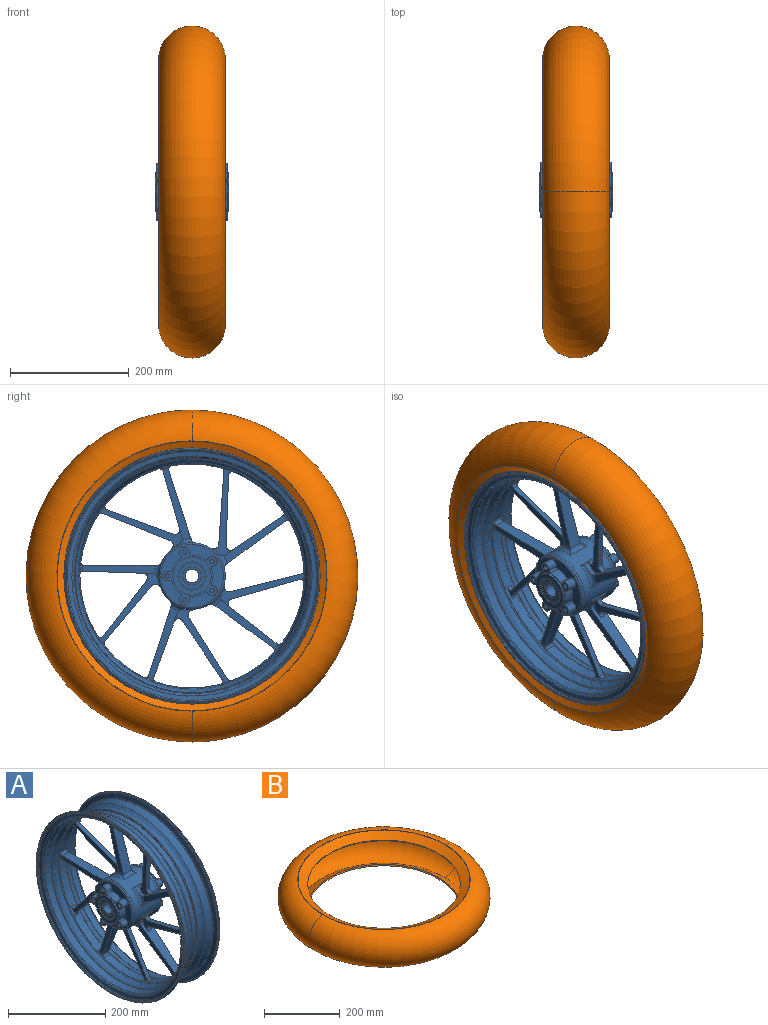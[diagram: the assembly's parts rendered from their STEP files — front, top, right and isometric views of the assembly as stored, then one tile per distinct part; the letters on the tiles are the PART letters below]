
ASSEMBLY  parts=2 mates=1
PART A: 286 faces, bbox 125.2x468.5x468.5 mm
  f0: cylinder r=11.66mm len=120.31mm, axis (1,0,0), area 8812.2mm2, adj f1,f2
  f1: plane 30.78x30.78mm, normal (1,0,0), area 317mm2, adj f0,f3
  f2: plane 30.78x30.78mm, normal (-1,0,0), area 317mm2, adj f0,f4
  f3: cylinder r=15.39mm len=30.78mm, axis (1,0,0), area 9mm2, adj f1,f5
  f4: cylinder r=15.39mm len=30.78mm, axis (-1,0,0), area 9mm2, adj f2,f6
  f5: plane 41.97x41.97mm, normal (1,0,0), area 639.4mm2, adj f3,f7
  f6: plane 41.97x41.97mm, normal (-1,0,0), area 639.4mm2, adj f4,f8
  f7: cylinder r=20.98mm len=41.97mm, axis (1,0,0), area 12.3mm2, adj f5,f9
  f8: cylinder r=20.98mm len=41.97mm, axis (-1,0,0), area 12.3mm2, adj f6,f10
  f9: plane 48.5x48.5mm, normal (1,0,0), area 463.8mm2, adj f7,f11
  f10: plane 48.5x48.5mm, normal (-1,0,0), area 463.8mm2, adj f8,f12
  f11: cylinder r=24.25mm len=48.5mm, axis (1,0,0), area 284.2mm2, adj f9,f13
  f12: cylinder r=24.25mm len=48.5mm, axis (1,0,0), area 284.2mm2, adj f10,f19
  f13: plane 64.35x64.35mm, normal (1,0,0), area 1405.2mm2, adj f11,f25
  f14: plane 7.46x7.46mm, normal (1,0,0), area 43.7mm2, adj f26
  f15: plane 7.46x7.46mm, normal (1,0,0), area 43.7mm2, adj f27
  f16: plane 7.46x7.46mm, normal (1,0,0), area 43.7mm2, adj f28
  f17: plane 7.46x7.46mm, normal (1,0,0), area 43.7mm2, adj f29
  f18: plane 7.46x7.46mm, normal (1,0,0), area 43.7mm2, adj f30,f31
  f19: plane 64.35x64.35mm, normal (-1,0,0), area 1405.2mm2, adj f12,f32
  f20: plane 7.46x7.46mm, normal (-1,0,0), area 43.7mm2, adj f33
  f21: plane 7.46x7.46mm, normal (-1,0,0), area 43.7mm2, adj f34
  f22: plane 7.46x7.46mm, normal (-1,0,0), area 43.7mm2, adj f35
  f23: plane 7.46x7.46mm, normal (-1,0,0), area 43.7mm2, adj f36
  f24: plane 7.46x7.46mm, normal (-1,0,0), area 43.7mm2, adj f37,f38
  f25: cylinder r=32.18mm len=64.35mm, axis (1,0,0), area 565.6mm2, adj f13,f39
  f26: cylinder r=3.73mm len=16.79mm, axis (-1,0,0), area 393.5mm2, adj f14,f39
  f27: cylinder r=3.73mm len=16.79mm, axis (-1,0,0), area 393.5mm2, adj f15,f39
  f28: cylinder r=3.73mm len=16.79mm, axis (-1,0,0), area 393.5mm2, adj f16,f39
  f29: cylinder r=3.73mm len=16.79mm, axis (-1,0,0), area 393.5mm2, adj f17,f39
  f30: cylinder r=3.73mm len=16.79mm, axis (-1,0,0), area 196.7mm2, adj f18,f31,f39
  f31: cylinder r=3.73mm len=16.79mm, axis (-1,0,0), area 196.7mm2, adj f18,f30,f39
  f32: cylinder r=32.18mm len=64.35mm, axis (1,0,0), area 565.6mm2, adj f19,f40
  f33: cylinder r=3.73mm len=16.79mm, axis (-1,0,0), area 393.5mm2, adj f20,f40
  f34: cylinder r=3.73mm len=16.79mm, axis (-1,0,0), area 393.5mm2, adj f21,f40
  f35: cylinder r=3.73mm len=16.79mm, axis (-1,0,0), area 393.5mm2, adj f22,f40
  f36: cylinder r=3.73mm len=16.79mm, axis (-1,0,0), area 393.5mm2, adj f23,f40
  f37: cylinder r=3.73mm len=16.79mm, axis (-1,0,0), area 196.7mm2, adj f24,f38,f40
  f38: cylinder r=3.73mm len=16.79mm, axis (-1,0,0), area 196.7mm2, adj f24,f37,f40
  f39: plane 96.61x92.71mm, normal (1,0,0), area 1483.4mm2, adj f25,f26,f27,f28,f29,f30,f31,f41
  f40: plane 96.61x92.71mm, normal (-1,0,0), area 1483.4mm2, adj f32,f33,f34,f35,f36,f37,f38,f63
  f41: cylinder r=34.97mm len=20.3mm, axis (1,0,0), area 430.9mm2, adj f39,f42,f62,f85
  f42: cylinder r=2.8mm len=16.79mm, axis (-1,0,0), area 46.7mm2, adj f39,f41,f43,f85
  f43: cylinder r=2.8mm len=16.79mm, axis (-1,0,0), area 38.8mm2, adj f39,f42,f44,f85
  f44: cylinder r=8.39mm len=16.79mm, axis (-1,0,0), area 116.4mm2, adj f39,f43,f45,f85
  f45: cylinder r=8.39mm len=16.79mm, axis (-1,0,0), area 470.5mm2, adj f39,f44,f46,f85
  f46: cylinder r=2.8mm len=16.79mm, axis (1,0,0), area 85.5mm2, adj f39,f45,f47,f85
  f47: cylinder r=34.97mm len=23.87mm, axis (1,0,0), area 430.9mm2, adj f39,f46,f48,f85
  f48: cylinder r=2.8mm len=16.79mm, axis (-1,0,0), area 85.5mm2, adj f39,f47,f49,f85
  f49: cylinder r=8.39mm len=16.79mm, axis (-1,0,0), area 586.8mm2, adj f39,f48,f50,f85
  f50: cylinder r=2.8mm len=16.79mm, axis (1,0,0), area 85.5mm2, adj f39,f49,f51,f85
  f51: cylinder r=34.97mm len=25.1mm, axis (1,0,0), area 430.9mm2, adj f39,f50,f52,f85
  f52: cylinder r=2.8mm len=16.79mm, axis (-1,0,0), area 85.5mm2, adj f39,f51,f53,f85
  f53: cylinder r=8.39mm len=16.79mm, axis (-1,0,0), area 586.8mm2, adj f39,f52,f54,f85
  f54: cylinder r=2.8mm len=16.79mm, axis (1,0,0), area 85.5mm2, adj f39,f53,f55,f85
  f55: cylinder r=34.97mm len=23.87mm, axis (1,0,0), area 430.9mm2, adj f39,f54,f56,f85
  f56: cylinder r=2.8mm len=16.79mm, axis (-1,0,0), area 85.5mm2, adj f39,f55,f57,f85
  f57: cylinder r=8.39mm len=16.79mm, axis (-1,0,0), area 586.8mm2, adj f39,f56,f58,f85
  f58: cylinder r=2.8mm len=16.79mm, axis (1,0,0), area 85.5mm2, adj f39,f57,f59,f85
  f59: cylinder r=34.97mm len=20.3mm, axis (1,0,0), area 430.9mm2, adj f39,f58,f60,f85
  f60: cylinder r=2.8mm len=16.79mm, axis (-1,0,0), area 85.5mm2, adj f39,f59,f61,f85
  f61: cylinder r=8.39mm len=16.79mm, axis (-1,0,0), area 586.8mm2, adj f39,f60,f62,f85
  f62: cylinder r=2.8mm len=16.79mm, axis (1,0,0), area 85.5mm2, adj f39,f41,f61,f85
  f63: cylinder r=34.97mm len=20.3mm, axis (1,0,0), area 430.9mm2, adj f40,f64,f84,f86
  f64: cylinder r=2.8mm len=16.79mm, axis (1,0,0), area 85.5mm2, adj f40,f63,f65,f86
  f65: cylinder r=8.39mm len=16.79mm, axis (-1,0,0), area 586.8mm2, adj f40,f64,f66,f86
  f66: cylinder r=2.8mm len=16.79mm, axis (-1,0,0), area 85.5mm2, adj f40,f65,f67,f86
  f67: cylinder r=34.97mm len=20.3mm, axis (1,0,0), area 430.9mm2, adj f40,f66,f68,f86
  f68: cylinder r=2.8mm len=16.79mm, axis (1,0,0), area 85.5mm2, adj f40,f67,f69,f86
  f69: cylinder r=8.39mm len=16.79mm, axis (-1,0,0), area 586.8mm2, adj f40,f68,f70,f86
  f70: cylinder r=2.8mm len=16.79mm, axis (-1,0,0), area 85.5mm2, adj f40,f69,f71,f86
  f71: cylinder r=34.97mm len=23.87mm, axis (1,0,0), area 430.9mm2, adj f40,f70,f72,f86
  f72: cylinder r=2.8mm len=16.79mm, axis (1,0,0), area 85.5mm2, adj f40,f71,f73,f86
  f73: cylinder r=8.39mm len=16.79mm, axis (-1,0,0), area 586.8mm2, adj f40,f72,f74,f86
  f74: cylinder r=2.8mm len=16.79mm, axis (-1,0,0), area 85.5mm2, adj f40,f73,f75,f86
  f75: cylinder r=34.97mm len=25.1mm, axis (1,0,0), area 430.9mm2, adj f40,f74,f76,f86
  f76: cylinder r=2.8mm len=16.79mm, axis (1,0,0), area 85.5mm2, adj f40,f75,f77,f86
  f77: cylinder r=8.39mm len=16.79mm, axis (-1,0,0), area 586.8mm2, adj f40,f76,f78,f86
  f78: cylinder r=2.8mm len=16.79mm, axis (-1,0,0), area 85.5mm2, adj f40,f77,f79,f86
  f79: cylinder r=34.97mm len=23.87mm, axis (1,0,0), area 430.9mm2, adj f40,f78,f80,f86
  f80: cylinder r=2.8mm len=16.79mm, axis (1,0,0), area 85.5mm2, adj f40,f79,f81,f86
  f81: cylinder r=8.39mm len=16.79mm, axis (-1,0,0), area 470.5mm2, adj f40,f80,f82,f86
  f82: cylinder r=8.39mm len=16.79mm, axis (-1,0,0), area 116.4mm2, adj f40,f81,f83,f86
  f83: cylinder r=2.8mm len=16.79mm, axis (-1,0,0), area 38.8mm2, adj f40,f82,f84,f86
  f84: cylinder r=2.8mm len=16.79mm, axis (-1,0,0), area 46.7mm2, adj f40,f63,f83,f86
  f85: plane 106.32x106.32mm, normal (1,0,0), area 3921.2mm2, adj f41,f42,f43,f44,f45,f46,f47,f48
  f86: plane 106.32x106.32mm, normal (-1,0,0), area 3921.2mm2, adj f63,f64,f65,f66,f67,f68,f69,f70
  f87: torus R=53.16mm, axis (1,0,0), area 758.5mm2, adj f85,f89,f91
  f88: torus R=53.16mm, axis (-1,0,0), area 758.5mm2, adj f86,f90,f92
  f89: torus R=53.16mm, axis (1,0,0), area 758.5mm2, adj f85,f87,f91
  f90: torus R=53.16mm, axis (-1,0,0), area 758.5mm2, adj f86,f88,f92
  f91: cylinder r=55.96mm len=111.91mm, axis (1,0,0), area 1639.5mm2, adj f87,f89,f104
  f92: cylinder r=55.96mm len=111.91mm, axis (1,0,0), area 1639.5mm2, adj f88,f90,f104
  f93: cylinder r=9.33mm len=37.91mm, axis (1,0,0), area 325.9mm2, adj f104,f105,f111,f112
  f94: plane 39.04x4.28mm, normal (0,0.94,0.34), area 104.7mm2, adj f96,f104,f114,f116,f117,f123
  f95: cylinder r=9.33mm len=37.91mm, axis (1,0,0), area 325.9mm2, adj f96,f104,f123,f124
  f96: torus R=63.42mm, axis (-1,0,0), area 325.2mm2, adj f94,f95,f104,f114,f115,f124,f133
  f97: plane 39.04x4.48mm, normal (0,-0.03,1), area 104.7mm2, adj f99,f104,f126,f128,f129,f136
  f98: cylinder r=9.33mm len=37.91mm, axis (1,0,0), area 325.9mm2, adj f99,f104,f136,f150
  f99: torus R=63.42mm, axis (-1,0,0), area 325.2mm2, adj f97,f98,f104,f129,f130,f149,f150
  f100: plane 39.04x4.35mm, normal (0,-0.96,0.28), area 104.7mm2, adj f102,f104,f138,f140,f141,f152
  f101: cylinder r=9.33mm len=37.91mm, axis (1,0,0), area 325.9mm2, adj f102,f104,f152,f163
  f102: torus R=63.42mm, axis (-1,0,0), area 325.2mm2, adj f100,f101,f104,f138,f139,f162,f163
  f103: plane 39.04x3.9mm, normal (0,-0.56,-0.83), area 104.7mm2, adj f104,f108,f154,f157,f158,f166
  f104: cylinder r=55.96mm len=111.91mm, axis (1,0,0), area 16231.7mm2, adj f91,f92,f93,f94,f95,f96,f97,f98
  f105: torus R=63.42mm, axis (-1,0,0), area 325.2mm2, adj f93,f104,f106,f112,f113,f168,f169
  f106: plane 39.04x3.78mm, normal (0,0.61,-0.79), area 104.7mm2, adj f104,f105,f111,f168,f171,f172
  f107: cylinder r=9.33mm len=37.91mm, axis (1,0,0), area 325.9mm2, adj f104,f108,f166,f182
  f108: torus R=63.42mm, axis (-1,0,0), area 325.3mm2, adj f103,f104,f107,f158,f159,f181,f182
  f109: torus R=194.62mm, axis (1,0,0), area 1109.6mm2, adj f110,f145,f183
  f110: torus R=194.62mm, axis (1,0,0), area 1109.6mm2, adj f109,f179,f183
  f111: torus R=63.42mm, axis (-1,0,0), area 325.2mm2, adj f93,f104,f106,f112,f172,f173,f184
  f112: plane 122.38x23.27mm, normal (0,0,1), area 2498.4mm2, adj f93,f105,f111,f113,f184,f185
  f113: cone r=0mm half-angle=88.7deg, axis (1,0,0), area 1400.3mm2, adj f105,f112,f147,f169,f174,f185,f186
  f114: cylinder r=57.79mm len=11.72mm, axis (-1,0,0), area 126.5mm2, adj f94,f96,f115,f187
  f115: cylinder r=9.33mm len=11.19mm, axis (-1,0,0), area 105.7mm2, adj f96,f114,f125,f133,f187
  f116: cylinder r=7.46mm len=12.25mm, axis (-1,0,0), area 138mm2, adj f94,f121,f187,f189
  f117: cylinder r=57.79mm len=11.72mm, axis (-1,0,0), area 126.5mm2, adj f94,f122,f123,f189
  f118: cylinder r=7.46mm len=10.01mm, axis (1,0,0), area 153mm2, adj f119,f125,f187,f189
  f119: plane 112.57x40.97mm, normal (0,-0.34,0.94), area 1117.3mm2, adj f118,f120,f187,f189
  f120: cylinder r=5.6mm len=9.33mm, axis (1,0,0), area 63.8mm2, adj f119,f187,f188,f189
  f121: plane 115x46.46mm, normal (0,0.37,-0.93), area 1156.7mm2, adj f116,f187,f189,f190
  f122: cylinder r=9.33mm len=11.19mm, axis (-1,0,0), area 105.7mm2, adj f117,f123,f125,f189,f192
  f123: torus R=63.42mm, axis (-1,0,0), area 325.2mm2, adj f94,f95,f104,f117,f122,f124,f192
  f124: plane 116.39x37.82mm, normal (0,-0.95,0.31), area 2498.4mm2, adj f95,f96,f123,f133,f134,f192
  f125: plane 113x33.11mm, normal (0,0.96,-0.28), area 2219.2mm2, adj f115,f118,f122,f133,f187,f189,f192,f193
  f126: cylinder r=57.79mm len=9.84mm, axis (-1,0,0), area 126.5mm2, adj f97,f135,f136,f194
  f127: plane 123.73x9.33mm, normal (0,1,0.07), area 1156.7mm2, adj f128,f194,f195,f196
  f128: cylinder r=7.46mm len=10.9mm, axis (-1,0,0), area 138mm2, adj f97,f127,f194,f196
  f129: cylinder r=57.79mm len=9.84mm, axis (-1,0,0), area 126.5mm2, adj f97,f99,f130,f196
  f130: cylinder r=9.33mm len=12.31mm, axis (-1,0,0), area 105.7mm2, adj f99,f129,f137,f149,f196
  f131: cylinder r=7.46mm len=11.63mm, axis (1,0,0), area 153mm2, adj f132,f137,f194,f196
  f132: plane 119.73x9.33mm, normal (0,-1,-0.03), area 1117.3mm2, adj f131,f194,f196,f197
  f133: cone r=0mm half-angle=88.7deg, axis (1,0,0), area 1400.3mm2, adj f96,f115,f124,f125,f134,f146,f193,f198
  f134: cylinder r=5.6mm len=17.75mm, axis (1,0,0), area 31.1mm2, adj f124,f133,f192,f198
  f135: cylinder r=9.33mm len=12.31mm, axis (-1,0,0), area 105.7mm2, adj f126,f136,f137,f194,f199
  f136: torus R=63.42mm, axis (-1,0,0), area 325.2mm2, adj f97,f98,f104,f126,f135,f150,f199
  f137: plane 97.6x66.15mm, normal (0,0.56,0.83), area 2219.2mm2, adj f130,f131,f135,f149,f194,f196,f199,f200
  f138: cylinder r=57.79mm len=12.18mm, axis (-1,0,0), area 126.5mm2, adj f100,f102,f139,f201
  f139: cylinder r=9.33mm len=12.23mm, axis (-1,0,0), area 105.7mm2, adj f102,f138,f153,f162,f201
  f140: cylinder r=7.46mm len=9.33mm, axis (-1,0,0), area 138mm2, adj f100,f144,f201,f203
  f141: cylinder r=57.79mm len=12.18mm, axis (-1,0,0), area 126.5mm2, adj f100,f151,f152,f203
  f142: cylinder r=7.46mm len=13.05mm, axis (1,0,0), area 153mm2, adj f143,f153,f201,f203
  f143: plane 115.16x33.02mm, normal (0,-0.28,-0.96), area 1117.3mm2, adj f142,f201,f202,f203
  f144: plane 120.35x30.01mm, normal (0,0.24,0.97), area 1156.7mm2, adj f140,f201,f203,f204
  f145: torus R=214.38mm, axis (1,0,0), area 8984mm2, adj f109,f179,f205
  f146: revolved ~21.47x8.32mm, area 56.3mm2, adj f133,f193,f198,f205
  f147: torus R=185.69mm, axis (1,0,0), area 49mm2, adj f113,f185,f186,f191,f205
  f148: revolved ~19.81x14.05mm, area 56.3mm2, adj f149,f200,f205,f206
  f149: cone r=0mm half-angle=88.7deg, axis (1,0,0), area 1400.3mm2, adj f99,f130,f137,f148,f150,f200,f206
  f150: plane 99x71.93mm, normal (0,-0.59,-0.81), area 2498.4mm2, adj f98,f99,f136,f149,f199,f206
  f151: cylinder r=9.33mm len=12.23mm, axis (-1,0,0), area 105.7mm2, adj f141,f152,f153,f203,f207
  f152: torus R=63.42mm, axis (-1,0,0), area 325.2mm2, adj f100,f101,f104,f141,f151,f163,f207
  f153: plane 92.82x72.73mm, normal (0,-0.62,0.79), area 2219.2mm2, adj f139,f142,f151,f162,f201,f203,f207,f208
  f154: cylinder r=57.79mm len=13.33mm, axis (-1,0,0), area 126.5mm2, adj f103,f165,f166,f209
  f155: plane 105.19x65.73mm, normal (0,-0.85,0.53), area 1156.7mm2, adj f156,f209,f210,f211
  f156: cylinder r=7.46mm len=9.33mm, axis (-1,0,0), area 60.7mm2, adj f155,f157,f209,f211
  f157: cylinder r=7.46mm len=9.33mm, axis (-1,0,0), area 77.3mm2, adj f103,f156,f209,f211
  f158: cylinder r=57.79mm len=13.33mm, axis (-1,0,0), area 126.5mm2, adj f103,f108,f159,f211
  f159: cylinder r=9.33mm len=10.94mm, axis (-1,0,0), area 105.7mm2, adj f108,f158,f164,f181,f211
  f160: cylinder r=7.46mm len=13.2mm, axis (1,0,0), area 153mm2, adj f161,f164,f209,f211
  f161: plane 99.32x66.99mm, normal (0,0.83,-0.56), area 1117.3mm2, adj f160,f209,f211,f212
  f162: cone r=0mm half-angle=88.7deg, axis (1,0,0), area 1400.3mm2, adj f102,f139,f153,f163,f178,f208,f213
  f163: plane 99x71.93mm, normal (0,0.59,-0.81), area 2498.4mm2, adj f101,f102,f152,f162,f207,f213
  f164: plane 109.5x39.86mm, normal (0,-0.94,-0.34), area 2219.2mm2, adj f159,f160,f165,f167,f181,f209,f211,f214
  f165: cylinder r=9.33mm len=10.94mm, axis (-1,0,0), area 105.7mm2, adj f154,f164,f166,f209,f214
  f166: torus R=63.42mm, axis (-1,0,0), area 325.5mm2, adj f103,f104,f107,f154,f165,f182,f214
  f167: cylinder r=5.6mm len=17.73mm, axis (1,0,0), area 34.5mm2, adj f164,f181,f214,f215
  f168: cylinder r=57.79mm len=13.17mm, axis (-1,0,0), area 126.5mm2, adj f105,f106,f169,f216
  f169: cylinder r=9.33mm len=9.4mm, axis (-1,0,0), area 105.7mm2, adj f105,f113,f168,f174,f216
  f170: plane 95.01x79.73mm, normal (0,-0.77,-0.64), area 1156.7mm2, adj f171,f177,f216,f218
  f171: cylinder r=7.46mm len=12.4mm, axis (-1,0,0), area 138mm2, adj f106,f170,f216,f218
  f172: cylinder r=57.79mm len=13.17mm, axis (-1,0,0), area 126.5mm2, adj f106,f111,f173,f218
  f173: cylinder r=9.33mm len=9.4mm, axis (-1,0,0), area 105.7mm2, adj f111,f172,f174,f184,f218
  f174: plane 117.45x23.83mm, normal (0,0.03,-1), area 2219.2mm2, adj f113,f169,f173,f175,f184,f186,f216,f218
  f175: cylinder r=7.46mm len=12.05mm, axis (1,0,0), area 153mm2, adj f174,f176,f216,f218
  f176: plane 94.4x73.76mm, normal (0,0.79,0.62), area 1117.3mm2, adj f175,f216,f217,f218
  f177: cylinder r=5.6mm len=9.33mm, axis (1,0,0), area 36.4mm2, adj f170,f216,f218,f219
  f178: revolved ~18.41x16.22mm, area 56.3mm2, adj f162,f208,f213,f220
  f179: torus R=214.38mm, axis (1,0,0), area 8984mm2, adj f110,f145,f220
  f180: revolved ~20.97x11.05mm, area 56.3mm2, adj f181,f215,f220,f221
  f181: cone r=0mm half-angle=88.7deg, axis (1,0,0), area 1438.6mm2, adj f108,f159,f164,f167,f180,f182,f215,f221
  f182: plane 116.39x37.82mm, normal (0,0.95,0.31), area 2498.4mm2, adj f107,f108,f166,f181,f214,f221
  f183: cone r=0mm half-angle=5deg, axis (-1,0,0), area 20053.6mm2, adj f109,f110,f222,f223
  f184: cone r=0mm half-angle=88.7deg, axis (-1,0,0), area 1400.3mm2, adj f111,f112,f173,f174,f185,f186,f224
  f185: cylinder r=5.6mm len=19.52mm, axis (1,0,0), area 160.6mm2, adj f112,f113,f147,f184,f191,f224
  f186: cylinder r=5.6mm len=19.59mm, axis (1,0,0), area 163.5mm2, adj f113,f147,f174,f184,f224,f233
  f187: plane 141.68x73.36mm, normal (-1,0,0), area 1648.3mm2, adj f114,f115,f116,f118,f119,f120,f121,f125
  f188: cylinder r=5.6mm len=9.33mm, axis (1,0,0), area 36mm2, adj f120,f187,f189,f225
  f189: plane 141.68x73.36mm, normal (1,0,0), area 1648.3mm2, adj f116,f117,f118,f119,f120,f121,f122,f125
  f190: cylinder r=5.6mm len=9.33mm, axis (1,0,0), area 71.8mm2, adj f121,f187,f189,f225
  f191: cylinder r=5.6mm len=19.59mm, axis (1,0,0), area 14mm2, adj f147,f185,f224,f225
  f192: cone r=0mm half-angle=88.7deg, axis (-1,0,0), area 1400.3mm2, adj f122,f123,f124,f125,f134,f193,f198,f226
  f193: cylinder r=5.6mm len=19.59mm, axis (1,0,0), area 163.5mm2, adj f125,f133,f146,f192,f225,f226
  f194: plane 148.01x35.2mm, normal (1,0,0), area 1648.3mm2, adj f126,f127,f128,f131,f132,f135,f137,f195
  f195: cylinder r=5.6mm len=9.33mm, axis (1,0,0), area 71.8mm2, adj f127,f194,f196,f227
  f196: plane 148.01x35.2mm, normal (-1,0,0), area 1648.3mm2, adj f127,f128,f129,f130,f131,f132,f137,f195
  f197: cylinder r=5.6mm len=9.33mm, axis (1,0,0), area 99.8mm2, adj f132,f194,f196,f227
  f198: cylinder r=5.6mm len=19.59mm, axis (1,0,0), area 142.9mm2, adj f133,f134,f146,f192,f226,f227
  f199: cone r=0mm half-angle=88.7deg, axis (-1,0,0), area 1400.3mm2, adj f135,f136,f137,f150,f200,f206,f228
  f200: cylinder r=5.6mm len=19.59mm, axis (1,0,0), area 163.5mm2, adj f137,f148,f149,f199,f227,f228
  f201: plane 140.98x61.17mm, normal (-1,0,0), area 1648.3mm2, adj f138,f139,f140,f142,f143,f144,f153,f202
  f202: cylinder r=5.6mm len=9.33mm, axis (1,0,0), area 99.8mm2, adj f143,f201,f203,f229
  f203: plane 140.98x61.17mm, normal (1,0,0), area 1648.3mm2, adj f140,f141,f142,f143,f144,f151,f153,f202
  f204: cylinder r=5.6mm len=9.33mm, axis (1,0,0), area 71.8mm2, adj f144,f201,f203,f229
  f205: torus R=188.06mm, axis (-1,0,0), area 1972.6mm2, adj f145,f146,f147,f148,f220,f225,f227,f229
  f206: cylinder r=5.6mm len=19.59mm, axis (1,0,0), area 174.1mm2, adj f148,f149,f150,f199,f228,f229
  f207: cone r=0mm half-angle=88.7deg, axis (-1,0,0), area 1400.3mm2, adj f151,f152,f153,f163,f208,f213,f230
  f208: cylinder r=5.6mm len=19.59mm, axis (1,0,0), area 163.5mm2, adj f153,f162,f178,f207,f229,f230
  f209: plane 126.95x96.79mm, normal (1,0,0), area 1648.3mm2, adj f154,f155,f156,f157,f160,f161,f164,f165
  f210: cylinder r=5.6mm len=9.33mm, axis (1,0,0), area 71.8mm2, adj f155,f209,f211,f231
  f211: plane 126.95x96.79mm, normal (-1,0,0), area 1648.3mm2, adj f155,f156,f157,f158,f159,f160,f161,f164
  f212: cylinder r=5.6mm len=9.33mm, axis (1,0,0), area 99.8mm2, adj f161,f209,f211,f231
  f213: cylinder r=5.6mm len=19.59mm, axis (1,0,0), area 174.1mm2, adj f162,f163,f178,f207,f230,f231
  f214: cone r=0mm half-angle=88.7deg, axis (-1,0,0), area 1438.6mm2, adj f164,f165,f166,f167,f182,f215,f221,f232
  f215: cylinder r=5.6mm len=19.59mm, axis (1,0,0), area 128.9mm2, adj f167,f180,f181,f214,f231,f232
  f216: plane 122.94x104.33mm, normal (-1,0,0), area 1648.3mm2, adj f168,f169,f170,f171,f174,f175,f176,f177
  f217: cylinder r=5.6mm len=9.33mm, axis (1,0,0), area 99.8mm2, adj f176,f216,f218,f233
  f218: plane 122.94x104.33mm, normal (1,0,0), area 1648.3mm2, adj f170,f171,f172,f173,f174,f175,f176,f177
  f219: cylinder r=5.6mm len=9.33mm, axis (1,0,0), area 35.3mm2, adj f177,f216,f218,f233
  f220: torus R=188.06mm, axis (-1,0,0), area 1972.6mm2, adj f178,f179,f180,f205,f229,f231,f233
  f221: cylinder r=5.6mm len=19.59mm, axis (1,0,0), area 174.1mm2, adj f180,f181,f182,f214,f232,f233
  f222: torus R=203.46mm, axis (1,0,0), area 3736.6mm2, adj f183,f223,f234
  f223: torus R=203.46mm, axis (1,0,0), area 3736.6mm2, adj f183,f222,f234
  f224: revolved ~21.48x4.79mm, area 49mm2, adj f184,f185,f186,f191,f235
  f225: cylinder r=188.85mm len=156.32mm, axis (1,0,0), area 4032.6mm2, adj f187,f188,f189,f190,f191,f193,f205,f235
  f226: revolved ~21.47x8.32mm, area 56.3mm2, adj f192,f193,f198,f235
  f227: cylinder r=188.85mm len=189.3mm, axis (1,0,0), area 4032.6mm2, adj f194,f195,f196,f197,f198,f200,f205,f235
  f228: revolved ~19.81x14.05mm, area 56.3mm2, adj f199,f200,f206,f235
  f229: cylinder r=188.85mm len=203.75mm, axis (1,0,0), area 4032.6mm2, adj f201,f202,f203,f204,f205,f206,f208,f220
  f230: revolved ~18.41x16.22mm, area 56.3mm2, adj f207,f208,f213,f236
  f231: cylinder r=188.85mm len=198.26mm, axis (1,0,0), area 4032.6mm2, adj f209,f210,f211,f212,f213,f215,f220,f236
  f232: revolved ~20.97x11.05mm, area 56.3mm2, adj f214,f215,f221,f236
  f233: cylinder r=188.85mm len=173.36mm, axis (1,0,0), area 4032.6mm2, adj f186,f205,f216,f217,f218,f219,f220,f221
  f234: cone r=0mm half-angle=78deg, axis (-1,0,0), area 9889.1mm2, adj f222,f223,f237,f238
  f235: torus R=188.06mm, axis (-1,0,0), area 1972.6mm2, adj f224,f225,f226,f227,f228,f229,f233,f236
  f236: torus R=188.06mm, axis (-1,0,0), area 1972.6mm2, adj f229,f230,f231,f232,f233,f235,f240
  f237: torus R=209.37mm, axis (1,0,0), area 2529.4mm2, adj f234,f238,f241
  f238: torus R=209.37mm, axis (1,0,0), area 2529.4mm2, adj f234,f237,f241
  f239: torus R=214.38mm, axis (1,0,0), area 8984mm2, adj f235,f240,f242
  f240: torus R=214.38mm, axis (1,0,0), area 8984mm2, adj f236,f239,f243
  f241: cylinder r=212.17mm len=424.34mm, axis (1,0,0), area 739.6mm2, adj f237,f238,f244
  f242: torus R=194.62mm, axis (1,0,0), area 1109.6mm2, adj f239,f243,f245
  f243: torus R=194.62mm, axis (1,0,0), area 1109.6mm2, adj f240,f242,f245
  f244: plane 428.07x428.07mm, normal (-1,0,0), area 2107.6mm2, adj f241,f246,f247
  f245: cone r=0mm half-angle=5deg, axis (1,0,0), area 20053.6mm2, adj f242,f243,f248,f249
  f246: torus R=214.03mm, axis (-1,0,0), area 1980.9mm2, adj f244,f247,f250
  f247: torus R=214.03mm, axis (-1,0,0), area 1980.9mm2, adj f244,f246,f251
  f248: torus R=203.46mm, axis (1,0,0), area 3736.6mm2, adj f245,f249,f252
  f249: torus R=203.46mm, axis (1,0,0), area 3736.6mm2, adj f245,f248,f252
  f250: torus R=214.97mm, axis (-1,0,0), area 992.1mm2, adj f246,f251,f253
  f251: torus R=214.97mm, axis (-1,0,0), area 992.1mm2, adj f247,f250,f253
  f252: cone r=0mm half-angle=78deg, axis (1,0,0), area 9889.1mm2, adj f248,f249,f254,f255
  f253: cylinder r=214.97mm len=429.93mm, axis (1,0,0), area 1050.5mm2, adj f250,f251,f256,f257
  f254: torus R=209.37mm, axis (1,0,0), area 2529.4mm2, adj f252,f255,f258
  f255: torus R=209.37mm, axis (1,0,0), area 2529.4mm2, adj f252,f254,f258
  f256: torus R=213.1mm, axis (-1,0,0), area 1710.7mm2, adj f253,f257,f259
  f257: torus R=213.1mm, axis (-1,0,0), area 1710.7mm2, adj f253,f256,f259
  f258: cylinder r=212.17mm len=424.34mm, axis (1,0,0), area 739.6mm2, adj f254,f255,f260
  f259: cone r=0mm half-angle=78deg, axis (-1,0,0), area 13941.2mm2, adj f256,f257,f261,f262
  f260: plane 428.07x428.07mm, normal (1,0,0), area 2107.6mm2, adj f258,f263,f264
  f261: torus R=203.46mm, axis (1,0,0), area 1509.3mm2, adj f259,f262,f265
  f262: torus R=203.46mm, axis (1,0,0), area 1509.3mm2, adj f259,f261,f265
  f263: torus R=214.03mm, axis (1,0,0), area 1980.9mm2, adj f260,f264,f266
  f264: torus R=214.03mm, axis (1,0,0), area 1980.9mm2, adj f260,f263,f267
  f265: cone r=0mm half-angle=5deg, axis (-1,0,0), area 22824.3mm2, adj f261,f262,f268,f269
  f266: torus R=214.97mm, axis (1,0,0), area 992.1mm2, adj f263,f267,f270
  f267: torus R=214.97mm, axis (1,0,0), area 992.1mm2, adj f264,f266,f270
  f268: torus R=214.38mm, axis (1,0,0), area 10414.5mm2, adj f265,f269,f271
  f269: torus R=214.38mm, axis (1,0,0), area 10414.5mm2, adj f265,f268,f272
  f270: cylinder r=214.97mm len=429.93mm, axis (1,0,0), area 1050.5mm2, adj f266,f267,f273,f274
  f271: torus R=214.38mm, axis (1,0,0), area 1706.7mm2, adj f268,f272,f275
  f272: torus R=214.38mm, axis (1,0,0), area 1706.7mm2, adj f269,f271,f275
  f273: torus R=213.1mm, axis (-1,0,0), area 1710.7mm2, adj f270,f274,f276
  f274: torus R=213.1mm, axis (-1,0,0), area 1710.7mm2, adj f270,f273,f276
  f275: plane 387.41x387.41mm, normal (1,0,0), area 3160.8mm2, adj f271,f272,f277
  f276: cone r=0mm half-angle=78deg, axis (1,0,0), area 13941.2mm2, adj f273,f274,f278,f279
  f277: cylinder r=190.82mm len=381.65mm, axis (1,0,0), area 16772.9mm2, adj f275,f280
  f278: torus R=203.46mm, axis (1,0,0), area 1509.3mm2, adj f276,f279,f282
  f279: torus R=203.46mm, axis (1,0,0), area 1509.3mm2, adj f276,f278,f282
  f280: plane 387.41x387.41mm, normal (-1,0,0), area 3160.8mm2, adj f277,f281,f283
  f281: torus R=214.38mm, axis (1,0,0), area 1706.7mm2, adj f280,f283,f284
  f282: cone r=0mm half-angle=5deg, axis (1,0,0), area 22824.3mm2, adj f278,f279,f284,f285
  f283: torus R=214.38mm, axis (1,0,0), area 1706.7mm2, adj f280,f281,f285
  f284: torus R=214.38mm, axis (1,0,0), area 10414.5mm2, adj f281,f282,f285
  f285: torus R=214.38mm, axis (1,0,0), area 10414.5mm2, adj f282,f283,f284
PART B: 14 faces, bbox 605.7x605.7x112.2 mm
  f0: cone r=0mm half-angle=60.9deg, axis (0,0,-1), area 38929.1mm2, adj f1,f2,f3
  f1: torus R=223.7mm, axis (0,0,1), area 126314mm2, adj f0,f2,f4
  f2: torus R=223.7mm, axis (0,0,1), area 126314mm2, adj f0,f1,f4
  f3: cone r=0mm half-angle=29.1deg, axis (0,0,1), area 4740.7mm2, adj f0,f5
  f4: cone r=0mm half-angle=60.9deg, axis (0,0,1), area 38929.1mm2, adj f1,f2,f7
  f5: cone r=0mm half-angle=60.9deg, axis (0,0,-1), area 39806.5mm2, adj f3,f6,f8
  f6: torus R=227.65mm, axis (0,0,-1), area 385.8mm2, adj f5,f8,f9
  f7: cone r=0mm half-angle=29.1deg, axis (0,0,-1), area 4740.7mm2, adj f4,f10
  f8: torus R=227.65mm, axis (0,0,-1), area 385.8mm2, adj f5,f6,f11
  f9: torus R=223.7mm, axis (0,0,1), area 137889.1mm2, adj f6,f11,f12
  f10: cone r=0mm half-angle=60.9deg, axis (0,0,1), area 39806.5mm2, adj f7,f12,f13
  f11: torus R=223.7mm, axis (0,0,1), area 137889.1mm2, adj f8,f9,f13
  f12: torus R=227.65mm, axis (0,0,-1), area 385.8mm2, adj f9,f10,f13
  f13: torus R=227.65mm, axis (0,0,-1), area 385.8mm2, adj f10,f11,f12
PLACE A at identity fixed
PLACE B rot(axis=(0,1,0),90deg) t=(0,0,0)mm
MATE fastened B.f9 <-> A.f0  axis (1,0,0) through (0,0,0)mm
